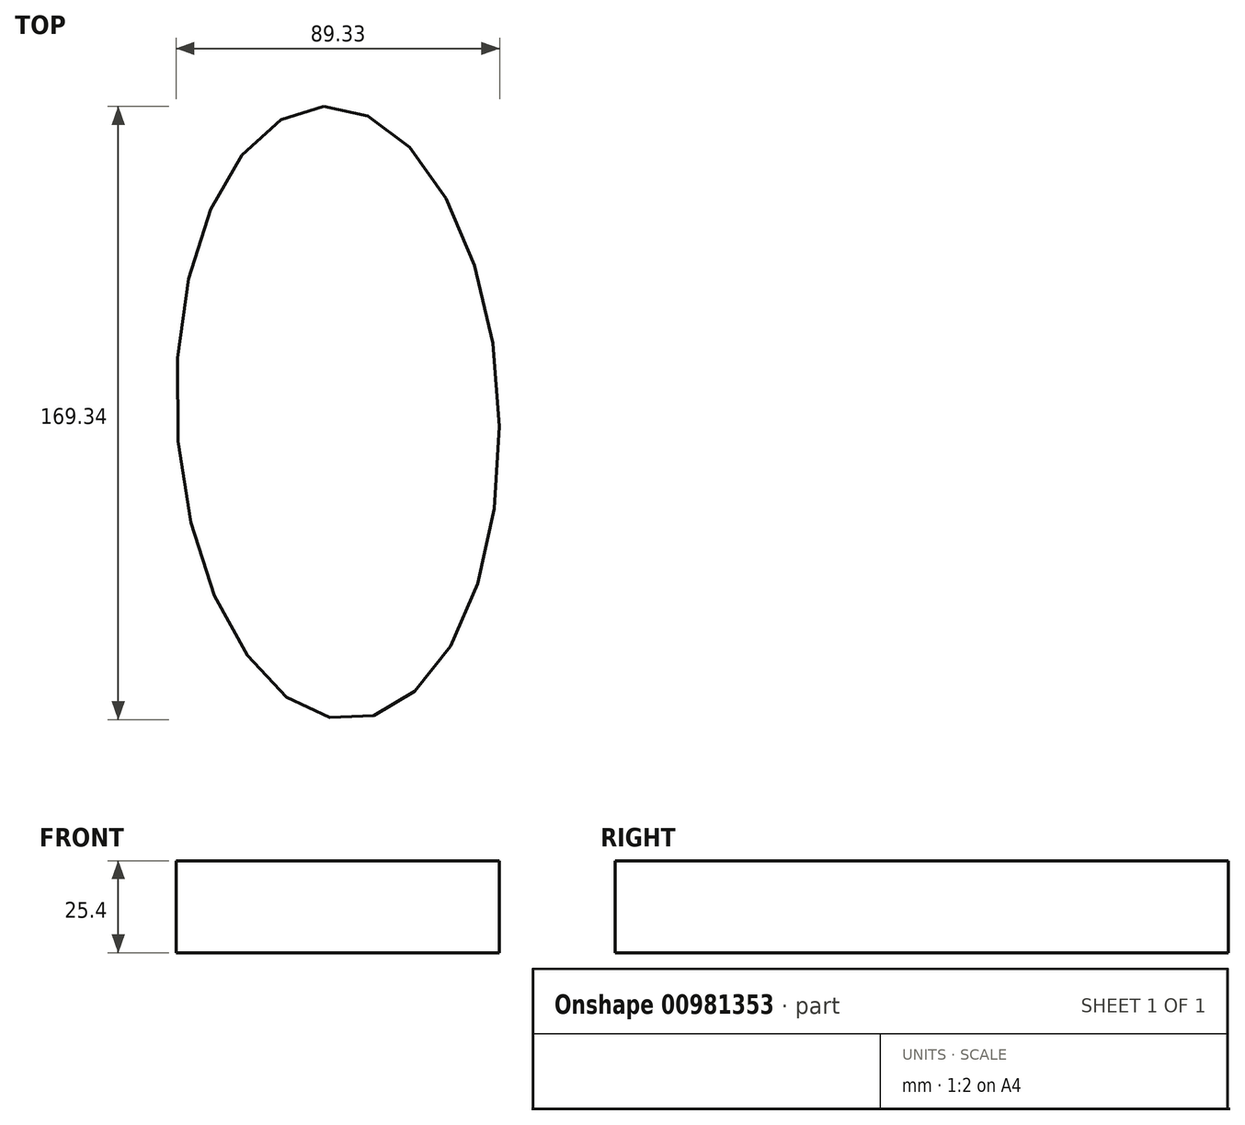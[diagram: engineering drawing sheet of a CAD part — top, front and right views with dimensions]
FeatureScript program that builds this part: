
annotation { "Feature Type Name" : "Feature", "Feature Type Description" : "" }
export const myFeature = defineFeature(function(context is Context, id is Id, definition is map)
    precondition{}
    {
        {
            var Q0;
            Q0=qCreatedBy(makeId("Top.planeOp"),FACE);
            var sketch = newSketch(context, id + "F0", { "sketchPlane" : qUnion([Q0])});
            skEllipse(sketch, "E0", {"center": v(-87.1, -44.2) * mm, "majorRadius": 84.74 * mm, "minorRadius": 44.54 * mm, "majorAxis": v(-0.05, 1)});
            skSolve(sketch);
        }
        {
            var Q0;
            Q0=makeQuery(id+"F0.imprint","IMPRINT",FACE,{"disambiguationData":[TD([[makeQuery(id+"F0.imprint","IMPRINT",EDGE,{"derivedFrom":sQuery(id+"F0.wireOp",EDGE,"E0")}),1.0]])]});
            extrude(context, id + "F1", {"entities" : qUnion([Q0]), "depth" : 25.4 * mm, "offsetDistance" : 25.4 * mm});
        }
    });
